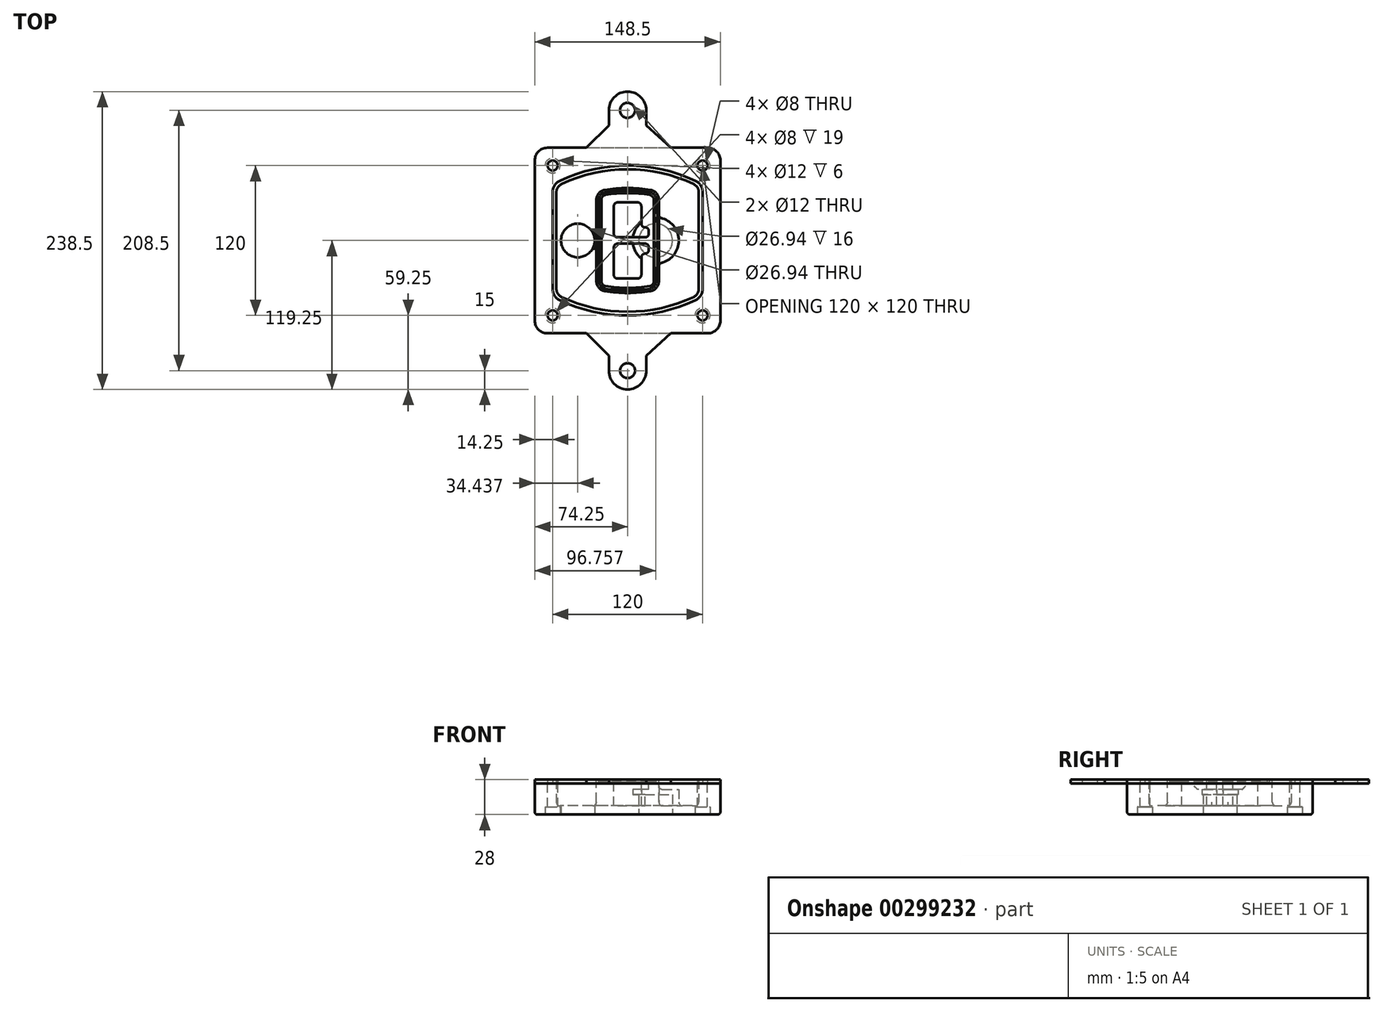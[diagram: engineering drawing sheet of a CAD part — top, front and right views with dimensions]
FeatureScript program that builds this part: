
annotation { "Feature Type Name" : "Feature", "Feature Type Description" : "" }
export const myFeature = defineFeature(function(context is Context, id is Id, definition is map)
    precondition{}
    {
        {
            var Q0;
            Q0=qCreatedBy(makeId("Top.planeOp"),FACE);
            var sketch = newSketch(context, id + "F0", { "sketchPlane" : qUnion([Q0])});
            skPoint(sketch, "E0.rect.middle", {"position": v(0, 0) * mm});
            skLineSegment(sketch, "E1.bottom", {"start": v(-64.25, -74.25) * mm, "end": v(64.25, -74.25) * mm});
            skLineSegment(sketch, "E1.top", {"start": v(-64.25, 74.25) * mm, "end": v(64.25, 74.25) * mm});
            skLineSegment(sketch, "E1.left", {"start": v(-74.25, -64.25) * mm, "end": v(-74.25, 64.25) * mm});
            skLineSegment(sketch, "E1.right", {"start": v(74.25, -64.25) * mm, "end": v(74.25, 64.25) * mm});
            skLineSegment(sketch, "E2", {"start": v(-74.25, 74.25) * mm, "end": v(74.25, -74.25) * mm, "construction": true});
            skLineSegment(sketch, "E3", {"start": v(74.25, 74.25) * mm, "end": v(-74.25, -74.25) * mm, "construction": true});
            skCircle(sketch, "E4", {"center": v(-60, 60) * mm, "radius": 4 * mm});
            skCircle(sketch, "E5", {"center": v(60, 60) * mm, "radius": 4 * mm});
            skCircle(sketch, "E6", {"center": v(60, -60) * mm, "radius": 4 * mm});
            skCircle(sketch, "E7", {"center": v(-60, -60) * mm, "radius": 4 * mm});
            skLineSegment(sketch, "E8", {"start": v(-60, 60) * mm, "end": v(60, 60) * mm, "construction": true});
            skLineSegment(sketch, "E9", {"start": v(60, 60) * mm, "end": v(60, -60) * mm, "construction": true});
            skLineSegment(sketch, "E10", {"start": v(60, -60) * mm, "end": v(-60, -60) * mm, "construction": true});
            skLineSegment(sketch, "E11", {"start": v(-60, -60) * mm, "end": v(-60, 60) * mm, "construction": true});
            skLineSegment(sketch, "E12", {"start": v(-60, 38.83) * mm, "end": v(-60, -38.83) * mm});
            skLineSegment(sketch, "E13", {"start": v(60, 38.83) * mm, "end": v(60, -38.83) * mm});
            skArc(sketch, "E14", {"start": v(54.26, 47.88) * mm, "mid": v(0, 60) * mm, "end": v(-54.26, 47.88) * mm});
            skArc(sketch, "E15", {"start": v(-54.26, -47.88) * mm, "mid": v(0, -60) * mm, "end": v(54.26, -47.88) * mm});
            skLineSegment(sketch, "E16", {"start": v(-60, 0) * mm, "end": v(60, 0) * mm, "construction": true});
            skPoint(sketch, "E17.visualSharp", {"position": v(-60, -45) * mm});
            skArc(sketch, "E17.filletArc", {"start": v(-60, -38.83) * mm, "mid": v(-58.44, -44.2) * mm, "end": v(-54.26, -47.88) * mm});
            skPoint(sketch, "E18.visualSharp", {"position": v(-60, 45) * mm});
            skArc(sketch, "E18.filletArc", {"start": v(-54.26, 47.88) * mm, "mid": v(-58.44, 44.2) * mm, "end": v(-60, 38.83) * mm});
            skPoint(sketch, "E19.visualSharp", {"position": v(60, 45) * mm});
            skArc(sketch, "E19.filletArc", {"start": v(60, 38.83) * mm, "mid": v(58.44, 44.2) * mm, "end": v(54.26, 47.88) * mm});
            skPoint(sketch, "E20.visualSharp", {"position": v(60, -45) * mm});
            skArc(sketch, "E20.filletArc", {"start": v(54.26, -47.88) * mm, "mid": v(58.44, -44.2) * mm, "end": v(60, -38.83) * mm});
            skPoint(sketch, "E21.visualSharp", {"position": v(-74.25, 74.25) * mm});
            skArc(sketch, "E21.filletArc", {"start": v(-64.25, 74.25) * mm, "mid": v(-71.32, 71.32) * mm, "end": v(-74.25, 64.25) * mm});
            skPoint(sketch, "E22.visualSharp", {"position": v(74.25, 74.25) * mm});
            skArc(sketch, "E22.filletArc", {"start": v(74.25, 64.25) * mm, "mid": v(71.32, 71.32) * mm, "end": v(64.25, 74.25) * mm});
            skPoint(sketch, "E23.visualSharp", {"position": v(74.25, -74.25) * mm});
            skArc(sketch, "E23.filletArc", {"start": v(64.25, -74.25) * mm, "mid": v(71.32, -71.32) * mm, "end": v(74.25, -64.25) * mm});
            skPoint(sketch, "E24.visualSharp", {"position": v(-74.25, -74.25) * mm});
            skArc(sketch, "E24.filletArc", {"start": v(-74.25, -64.25) * mm, "mid": v(-71.32, -71.32) * mm, "end": v(-64.25, -74.25) * mm});
            skArc(sketch, "E25.0", {"start": v(57, 38.83) * mm, "mid": v(55.9, 42.58) * mm, "end": v(52.98, 45.17) * mm});
            skLineSegment(sketch, "E25.1", {"start": v(57, 38.83) * mm, "end": v(57, -38.83) * mm});
            skArc(sketch, "E25.2", {"start": v(52.98, -45.17) * mm, "mid": v(55.9, -42.58) * mm, "end": v(57, -38.83) * mm});
            skArc(sketch, "E25.3", {"start": v(-52.98, -45.17) * mm, "mid": v(0, -57) * mm, "end": v(52.98, -45.17) * mm});
            skArc(sketch, "E25.4", {"start": v(-57, -38.83) * mm, "mid": v(-55.9, -42.58) * mm, "end": v(-52.98, -45.17) * mm});
            skArc(sketch, "E25.5", {"start": v(52.98, 45.17) * mm, "mid": v(0, 57) * mm, "end": v(-52.98, 45.17) * mm});
            skLineSegment(sketch, "E25.6", {"start": v(-57, 38.83) * mm, "end": v(-57, -38.83) * mm});
            skArc(sketch, "E25.7", {"start": v(-52.98, 45.17) * mm, "mid": v(-55.9, 42.58) * mm, "end": v(-57, 38.83) * mm});
            skArc(sketch, "E26.0", {"start": v(-55.96, 51.5) * mm, "mid": v(-61.82, 46.33) * mm, "end": v(-64, 38.83) * mm});
            skArc(sketch, "E26.1", {"start": v(55.96, 51.5) * mm, "mid": v(0, 64) * mm, "end": v(-55.96, 51.5) * mm});
            skArc(sketch, "E26.2", {"start": v(64, 38.83) * mm, "mid": v(61.82, 46.33) * mm, "end": v(55.96, 51.5) * mm});
            skLineSegment(sketch, "E26.3", {"start": v(64, 38.83) * mm, "end": v(64, -38.83) * mm});
            skArc(sketch, "E26.4", {"start": v(55.96, -51.5) * mm, "mid": v(61.82, -46.33) * mm, "end": v(64, -38.83) * mm});
            skLineSegment(sketch, "E26.5", {"start": v(-64, 38.83) * mm, "end": v(-64, -38.83) * mm});
            skArc(sketch, "E26.6", {"start": v(-55.96, -51.5) * mm, "mid": v(0, -64) * mm, "end": v(55.96, -51.5) * mm});
            skArc(sketch, "E26.7", {"start": v(-64, -38.83) * mm, "mid": v(-61.82, -46.33) * mm, "end": v(-55.96, -51.5) * mm});
            skSolve(sketch);
        }
        {
            var Q0;
            Q0=makeQuery(id+"F0.imprint","IMPRINT",FACE,{"disambiguationData":[TD([[makeQuery(id+"F0.imprint","IMPRINT",EDGE,{"derivedFrom":sQuery(id+"F0.wireOp",EDGE,"E1.bottom")}),1.0]])]});
            var Q1;
            Q1=makeQuery(id+"F0.imprint","IMPRINT",FACE,{"disambiguationData":[TD([[makeQuery(id+"F0.imprint","IMPRINT",EDGE,{"derivedFrom":sQuery(id+"F0.wireOp",EDGE,"E12")}),1.0]])]});
            var Q2;
            Q2=makeQuery(id+"F0.imprint","IMPRINT",FACE,{"disambiguationData":[TD([[makeQuery(id+"F0.imprint","IMPRINT",EDGE,{"derivedFrom":sQuery(id+"F0.wireOp",EDGE,"E25.0")}),1.0]])]});
            var Q3;
            Q3=makeQuery(id+"F0.imprint","IMPRINT",FACE,{"disambiguationData":[TD([[makeQuery(id+"F0.imprint","IMPRINT",EDGE,{"derivedFrom":sQuery(id+"F0.wireOp",EDGE,"E12")}),-1.0]])]});
            extrude(context, id + "F1", {"entities" : qUnion([Q0, Q1, Q2, Q3]), "oppositeDirection" : true, "depth" : 25 * mm});
        }
        {
            var Q0;
            Q0=makeQuery(id+"F0.imprint","IMPRINT",FACE,{"disambiguationData":[TD([[makeQuery(id+"F0.imprint","IMPRINT",EDGE,{"derivedFrom":sQuery(id+"F0.wireOp",EDGE,"E12")}),1.0]])]});
            extrude(context, id + "F2", {"entities" : qUnion([Q0]), "operationType" : NewBodyOperationType.ADD, "depth" : 3 * mm});
        }
        {
            var Q0;
            Q0=makeQuery(id+"F0.imprint","IMPRINT",FACE,{"disambiguationData":[TD([[makeQuery(id+"F0.imprint","IMPRINT",EDGE,{"derivedFrom":sQuery(id+"F0.wireOp",EDGE,"E25.0")}),1.0]])]});
            extrude(context, id + "F3", {"entities" : qUnion([Q0]), "operationType" : NewBodyOperationType.REMOVE, "oppositeDirection" : true, "depth" : 18 * mm});
        }
        {
            var Q0;
            Q0=makeQuery(id+"F2.opExtrude","CAP_FACE",FACE,{"disambiguationData":[OSD([sQuery(id+"F0.wireOp",EDGE,"E12"),sQuery(id+"F0.wireOp",EDGE,"E13"),sQuery(id+"F0.wireOp",EDGE,"E14"),sQuery(id+"F0.wireOp",EDGE,"E15"),sQuery(id+"F0.wireOp",EDGE,"E17.filletArc"),sQuery(id+"F0.wireOp",EDGE,"E18.filletArc"),sQuery(id+"F0.wireOp",EDGE,"E19.filletArc"),sQuery(id+"F0.wireOp",EDGE,"E20.filletArc"),sQuery(id+"F0.wireOp",EDGE,"E25.0"),sQuery(id+"F0.wireOp",EDGE,"E25.1"),sQuery(id+"F0.wireOp",EDGE,"E25.2"),sQuery(id+"F0.wireOp",EDGE,"E25.3"),sQuery(id+"F0.wireOp",EDGE,"E25.4"),sQuery(id+"F0.wireOp",EDGE,"E25.5"),sQuery(id+"F0.wireOp",EDGE,"E25.6"),sQuery(id+"F0.wireOp",EDGE,"E25.7")])],"isStart":false});
            var sketch = newSketch(context, id + "F4", { "sketchPlane" : qUnion([Q0])});
            skArc(sketch, "E27.0", {"start": v(-18.34, -40.45) * mm, "mid": v(0, -42) * mm, "end": v(18.34, -40.45) * mm});
            skArc(sketch, "E28.0", {"start": v(18.34, 40.45) * mm, "mid": v(0, 42) * mm, "end": v(-18.34, 40.45) * mm});
            skLineSegment(sketch, "E29", {"start": v(-25, 32.57) * mm, "end": v(-25, -32.57) * mm});
            skLineSegment(sketch, "E30", {"start": v(25, 32.57) * mm, "end": v(25, -32.57) * mm});
            skLineSegment(sketch, "E31", {"start": v(-25, 39.1) * mm, "end": v(25, 39.1) * mm, "construction": true});
            skLineSegment(sketch, "E32", {"start": v(-25, -39.1) * mm, "end": v(25, -39.1) * mm, "construction": true});
            skPoint(sketch, "E33.visualSharp", {"position": v(-25, 39.1) * mm});
            skArc(sketch, "E33.filletArc", {"start": v(-18.34, 40.45) * mm, "mid": v(-23.11, 37.73) * mm, "end": v(-25, 32.57) * mm});
            skPoint(sketch, "E34.visualSharp", {"position": v(25, 39.1) * mm});
            skArc(sketch, "E34.filletArc", {"start": v(25, 32.57) * mm, "mid": v(23.11, 37.73) * mm, "end": v(18.34, 40.45) * mm});
            skPoint(sketch, "E35.visualSharp", {"position": v(25, -39.1) * mm});
            skArc(sketch, "E35.filletArc", {"start": v(18.34, -40.45) * mm, "mid": v(23.11, -37.73) * mm, "end": v(25, -32.57) * mm});
            skPoint(sketch, "E36.visualSharp", {"position": v(-25, -39.1) * mm});
            skArc(sketch, "E36.filletArc", {"start": v(-25, -32.57) * mm, "mid": v(-23.11, -37.73) * mm, "end": v(-18.34, -40.45) * mm});
            skArc(sketch, "E37.0", {"start": v(52.98, 45.17) * mm, "mid": v(0, 57) * mm, "end": v(-52.98, 45.17) * mm});
            skArc(sketch, "E37.1", {"start": v(-52.98, 45.17) * mm, "mid": v(-55.9, 42.58) * mm, "end": v(-57, 38.83) * mm});
            skLineSegment(sketch, "E37.2", {"start": v(-57, 38.83) * mm, "end": v(-57, -38.83) * mm});
            skArc(sketch, "E37.3", {"start": v(-57, -38.83) * mm, "mid": v(-55.9, -42.58) * mm, "end": v(-52.98, -45.17) * mm});
            skArc(sketch, "E37.4", {"start": v(-52.98, -45.17) * mm, "mid": v(0, -57) * mm, "end": v(52.98, -45.17) * mm});
            skArc(sketch, "E37.5", {"start": v(52.98, -45.17) * mm, "mid": v(55.9, -42.58) * mm, "end": v(57, -38.83) * mm});
            skLineSegment(sketch, "E37.6", {"start": v(57, 38.83) * mm, "end": v(57, -38.83) * mm});
            skArc(sketch, "E37.7", {"start": v(57, 38.83) * mm, "mid": v(55.9, 42.58) * mm, "end": v(52.98, 45.17) * mm});
            skLineSegment(sketch, "E38.0", {"start": v(23, 32.57) * mm, "end": v(23, -32.57) * mm});
            skArc(sketch, "E38.1", {"start": v(18, -38.48) * mm, "mid": v(21.58, -36.44) * mm, "end": v(23, -32.57) * mm});
            skArc(sketch, "E38.2", {"start": v(-18, -38.48) * mm, "mid": v(0, -40) * mm, "end": v(18, -38.48) * mm});
            skArc(sketch, "E38.3", {"start": v(-23, -32.57) * mm, "mid": v(-21.58, -36.44) * mm, "end": v(-18, -38.48) * mm});
            skLineSegment(sketch, "E38.4", {"start": v(-23, 32.57) * mm, "end": v(-23, -32.57) * mm});
            skArc(sketch, "E38.5", {"start": v(23, 32.57) * mm, "mid": v(21.58, 36.44) * mm, "end": v(18, 38.48) * mm});
            skArc(sketch, "E38.6", {"start": v(-18, 38.48) * mm, "mid": v(-21.58, 36.44) * mm, "end": v(-23, 32.57) * mm});
            skArc(sketch, "E38.7", {"start": v(18, 38.48) * mm, "mid": v(0, 40) * mm, "end": v(-18, 38.48) * mm});
            skArc(sketch, "E39.0", {"start": v(21, 32.57) * mm, "mid": v(20.06, 35.15) * mm, "end": v(17.67, 36.5) * mm});
            skLineSegment(sketch, "E39.1", {"start": v(21, 32.57) * mm, "end": v(21, -32.57) * mm});
            skArc(sketch, "E39.2", {"start": v(17.67, -36.5) * mm, "mid": v(20.06, -35.15) * mm, "end": v(21, -32.57) * mm});
            skArc(sketch, "E39.3", {"start": v(-17.67, -36.5) * mm, "mid": v(0, -38) * mm, "end": v(17.67, -36.5) * mm});
            skArc(sketch, "E39.4", {"start": v(-21, -32.57) * mm, "mid": v(-20.06, -35.15) * mm, "end": v(-17.67, -36.5) * mm});
            skArc(sketch, "E39.5", {"start": v(17.67, 36.5) * mm, "mid": v(0, 38) * mm, "end": v(-17.67, 36.5) * mm});
            skLineSegment(sketch, "E39.6", {"start": v(-21, 32.57) * mm, "end": v(-21, -32.57) * mm});
            skArc(sketch, "E39.7", {"start": v(-17.67, 36.5) * mm, "mid": v(-20.06, 35.15) * mm, "end": v(-21, 32.57) * mm});
            skLineSegment(sketch, "E40", {"start": v(-25, 0) * mm, "end": v(25, 0) * mm, "construction": true});
            skLineSegment(sketch, "E41", {"start": v(-11, 5.5) * mm, "end": v(-11, 27.5) * mm});
            skLineSegment(sketch, "E42", {"start": v(-8, 30.5) * mm, "end": v(8, 30.5) * mm});
            skLineSegment(sketch, "E43", {"start": v(11, 27.5) * mm, "end": v(11, 13.5) * mm});
            skLineSegment(sketch, "E44", {"start": v(14, 10.5) * mm, "end": v(14, 10.5) * mm});
            skLineSegment(sketch, "E45", {"start": v(17, 7.5) * mm, "end": v(17, 5.5) * mm});
            skLineSegment(sketch, "E46", {"start": v(14, 2.5) * mm, "end": v(-8, 2.5) * mm});
            skPoint(sketch, "E47.visualSharp", {"position": v(-11, 30.5) * mm});
            skArc(sketch, "E47.filletArc", {"start": v(-8, 30.5) * mm, "mid": v(-10.12, 29.62) * mm, "end": v(-11, 27.5) * mm});
            skPoint(sketch, "E48.visualSharp", {"position": v(11, 30.5) * mm});
            skArc(sketch, "E48.filletArc", {"start": v(11, 27.5) * mm, "mid": v(10.12, 29.62) * mm, "end": v(8, 30.5) * mm});
            skPoint(sketch, "E49.visualSharp", {"position": v(11, 10.5) * mm});
            skArc(sketch, "E49.filletArc", {"start": v(11, 13.5) * mm, "mid": v(11.88, 11.38) * mm, "end": v(14, 10.5) * mm});
            skPoint(sketch, "E50.visualSharp", {"position": v(17, 10.5) * mm});
            skArc(sketch, "E50.filletArc", {"start": v(17, 7.5) * mm, "mid": v(16.12, 9.62) * mm, "end": v(14, 10.5) * mm});
            skPoint(sketch, "E51.visualSharp", {"position": v(17, 2.5) * mm});
            skArc(sketch, "E51.filletArc", {"start": v(14, 2.5) * mm, "mid": v(16.12, 3.38) * mm, "end": v(17, 5.5) * mm});
            skPoint(sketch, "E52.visualSharp", {"position": v(-11, 2.5) * mm});
            skArc(sketch, "E52.filletArc", {"start": v(-11, 5.5) * mm, "mid": v(-10.12, 3.38) * mm, "end": v(-8, 2.5) * mm});
            skLineSegment(sketch, "E53.0.MirrorCS", {"start": v(14, -2.5) * mm, "end": v(-8, -2.5) * mm});
            skArc(sketch, "E54.0.MirrorCS", {"start": v(-11, -5.5) * mm, "mid": v(-10.12, -3.38) * mm, "end": v(-8, -2.5) * mm});
            skLineSegment(sketch, "E55.0.MirrorCS", {"start": v(-11, -5.5) * mm, "end": v(-11, -27.5) * mm});
            skArc(sketch, "E56.0.MirrorCS", {"start": v(-8, -30.5) * mm, "mid": v(-10.12, -29.62) * mm, "end": v(-11, -27.5) * mm});
            skLineSegment(sketch, "E57.0.MirrorCS", {"start": v(-8, -30.5) * mm, "end": v(8, -30.5) * mm});
            skArc(sketch, "E58.0.MirrorCS", {"start": v(11, -27.5) * mm, "mid": v(10.12, -29.62) * mm, "end": v(8, -30.5) * mm});
            skLineSegment(sketch, "E59.0.MirrorCS", {"start": v(11, -27.5) * mm, "end": v(11, -13.5) * mm});
            skArc(sketch, "E60.0.MirrorCS", {"start": v(11, -13.5) * mm, "mid": v(11.88, -11.38) * mm, "end": v(14, -10.5) * mm});
            skArc(sketch, "E61.0.MirrorCS", {"start": v(17, -7.5) * mm, "mid": v(16.12, -9.62) * mm, "end": v(14, -10.5) * mm});
            skLineSegment(sketch, "E62.0.MirrorCS", {"start": v(17, -7.5) * mm, "end": v(17, -5.5) * mm});
            skArc(sketch, "E63.0.MirrorCS", {"start": v(14, -2.5) * mm, "mid": v(16.12, -3.38) * mm, "end": v(17, -5.5) * mm});
            skSolve(sketch);
        }
        {
            var Q0;
            Q0=makeQuery(id+"F4.imprint","IMPRINT",FACE,{"disambiguationData":[TD([[makeQuery(id+"F4.imprint","IMPRINT",EDGE,{"derivedFrom":sQuery(id+"F4.wireOp",EDGE,"E27.0")}),1.0]])]});
            var Q1;
            Q1=makeQuery(id+"F4.imprint","IMPRINT",FACE,{"disambiguationData":[TD([[makeQuery(id+"F4.imprint","IMPRINT",EDGE,{"derivedFrom":sQuery(id+"F4.wireOp",EDGE,"E38.0")}),-1.0]])]});
            var Q2;
            Q2=makeQuery(id+"F4.imprint","IMPRINT",FACE,{"disambiguationData":[TD([[makeQuery(id+"F4.imprint","IMPRINT",EDGE,{"derivedFrom":sQuery(id+"F4.wireOp",EDGE,"E39.0")}),1.0]])]});
            extrude(context, id + "F5", {"entities" : qUnion([Q0, Q1, Q2]), "operationType" : NewBodyOperationType.ADD, "endBound" : BoundingType.UP_TO_NEXT, "oppositeDirection" : true, "depth" : 25 * mm});
        }
        {
            var Q0;
            Q0=makeQuery(id+"F4.imprint","IMPRINT",FACE,{"disambiguationData":[TD([[makeQuery(id+"F4.imprint","IMPRINT",EDGE,{"derivedFrom":sQuery(id+"F4.wireOp",EDGE,"E38.0")}),-1.0]])]});
            extrude(context, id + "F6", {"entities" : qUnion([Q0]), "operationType" : NewBodyOperationType.REMOVE, "oppositeDirection" : true, "depth" : 2 * mm});
        }
        {
            var Q0;
            Q0=makeQuery(id+"F1.opExtrude","CAP_FACE",FACE,{"disambiguationData":[OSD([sQuery(id+"F0.wireOp",EDGE,"E1.bottom"),sQuery(id+"F0.wireOp",EDGE,"E1.top"),sQuery(id+"F0.wireOp",EDGE,"E1.left"),sQuery(id+"F0.wireOp",EDGE,"E1.right"),sQuery(id+"F0.wireOp",EDGE,"E4"),sQuery(id+"F0.wireOp",EDGE,"E5"),sQuery(id+"F0.wireOp",EDGE,"E6"),sQuery(id+"F0.wireOp",EDGE,"E7"),sQuery(id+"F0.wireOp",EDGE,"E21.filletArc"),sQuery(id+"F0.wireOp",EDGE,"E22.filletArc"),sQuery(id+"F0.wireOp",EDGE,"E23.filletArc"),sQuery(id+"F0.wireOp",EDGE,"E24.filletArc")])],"isStart":false});
            var sketch = newSketch(context, id + "F7", { "sketchPlane" : qUnion([Q0])});
            skCircle(sketch, "E64", {"center": v(22.5, 0) * mm, "radius": 13.47 * mm});
            skCircle(sketch, "E65", {"center": v(-39.81, 0) * mm, "radius": 13.47 * mm});
            skLineSegment(sketch, "E66", {"start": v(74.25, 0) * mm, "end": v(-74.25, 0) * mm});
            skCircle(sketch, "E67", {"center": v(22.5, 0) * mm, "radius": 18.47 * mm});
            skCircle(sketch, "E68", {"center": v(60, -60) * mm, "radius": 6 * mm});
            skCircle(sketch, "E69", {"center": v(-60, -60) * mm, "radius": 6 * mm});
            skCircle(sketch, "E70", {"center": v(-60, 60) * mm, "radius": 6 * mm});
            skCircle(sketch, "E71", {"center": v(60, 60) * mm, "radius": 6 * mm});
            skSolve(sketch);
        }
        {
            var Q0;
            {var subQ1=sQuery(id+"F7.wireOp",EDGE,"E66");var subQ4=sQuery(id+"F7.wireOp",EDGE,"E64");var subQ6=makeQuery(id+"F7.imprint","INTERSECT",VERTEX,{"disambiguationData":[OD(0.0)],"derivedFrom":[subQ4,subQ1]});Q0=makeQuery(id+"F7.imprint","IMPRINT",FACE,{"disambiguationData":[TD([[makeQuery(id+"F7.imprint","IMPRINT",EDGE,{"disambiguationData":[TD([[subQ6,-1.0]])],"derivedFrom":subQ4}),-1.0]])]});}
            var Q1;
            {var subQ0=sQuery(id+"F7.wireOp",EDGE,"E66");var subQ1=sQuery(id+"F7.wireOp",EDGE,"E64");var subQ3=makeQuery(id+"F7.imprint","INTERSECT",VERTEX,{"disambiguationData":[OD(0.0)],"derivedFrom":[subQ1,subQ0]});Q1=makeQuery(id+"F7.imprint","IMPRINT",FACE,{"disambiguationData":[TD([[makeQuery(id+"F7.imprint","IMPRINT",EDGE,{"disambiguationData":[TD([[subQ3,-1.0]])],"derivedFrom":subQ1}),1.0]])]});}
            var Q2;
            {var subQ0=sQuery(id+"F7.wireOp",EDGE,"E66");var subQ1=sQuery(id+"F7.wireOp",EDGE,"E64");var subQ3=makeQuery(id+"F7.imprint","INTERSECT",VERTEX,{"disambiguationData":[OD(0.0)],"derivedFrom":[subQ1,subQ0]});Q2=makeQuery(id+"F7.imprint","IMPRINT",FACE,{"disambiguationData":[TD([[makeQuery(id+"F7.imprint","IMPRINT",EDGE,{"disambiguationData":[TD([[subQ3,1.0]])],"derivedFrom":subQ1}),1.0]])]});}
            var Q3;
            {var subQ1=sQuery(id+"F7.wireOp",EDGE,"E66");var subQ4=sQuery(id+"F7.wireOp",EDGE,"E64");var subQ6=makeQuery(id+"F7.imprint","INTERSECT",VERTEX,{"disambiguationData":[OD(0.0)],"derivedFrom":[subQ4,subQ1]});Q3=makeQuery(id+"F7.imprint","IMPRINT",FACE,{"disambiguationData":[TD([[makeQuery(id+"F7.imprint","IMPRINT",EDGE,{"disambiguationData":[TD([[subQ6,1.0]])],"derivedFrom":subQ4}),-1.0]])]});}
            extrude(context, id + "F8", {"entities" : qUnion([Q0, Q1, Q2, Q3]), "operationType" : NewBodyOperationType.ADD, "oppositeDirection" : true, "depth" : 20 * mm});
        }
        {
            var Q0;
            {var subQ0=sQuery(id+"F7.wireOp",EDGE,"E66");var subQ1=sQuery(id+"F7.wireOp",EDGE,"E64");var subQ3=makeQuery(id+"F7.imprint","INTERSECT",VERTEX,{"disambiguationData":[OD(0.0)],"derivedFrom":[subQ1,subQ0]});Q0=makeQuery(id+"F7.imprint","IMPRINT",FACE,{"disambiguationData":[TD([[makeQuery(id+"F7.imprint","IMPRINT",EDGE,{"disambiguationData":[TD([[subQ3,-1.0]])],"derivedFrom":subQ1}),1.0]])]});}
            var Q1;
            {var subQ0=sQuery(id+"F7.wireOp",EDGE,"E66");var subQ1=sQuery(id+"F7.wireOp",EDGE,"E64");var subQ3=makeQuery(id+"F7.imprint","INTERSECT",VERTEX,{"disambiguationData":[OD(0.0)],"derivedFrom":[subQ1,subQ0]});Q1=makeQuery(id+"F7.imprint","IMPRINT",FACE,{"disambiguationData":[TD([[makeQuery(id+"F7.imprint","IMPRINT",EDGE,{"disambiguationData":[TD([[subQ3,1.0]])],"derivedFrom":subQ1}),1.0]])]});}
            extrude(context, id + "F9", {"entities" : qUnion([Q0, Q1]), "operationType" : NewBodyOperationType.REMOVE, "oppositeDirection" : true, "depth" : 16 * mm});
        }
        {
            var Q0;
            {var subQ0=sQuery(id+"F7.wireOp",EDGE,"E66");var subQ1=sQuery(id+"F7.wireOp",EDGE,"E65");var subQ3=makeQuery(id+"F7.imprint","INTERSECT",VERTEX,{"disambiguationData":[OD(0.0)],"derivedFrom":[subQ1,subQ0]});Q0=makeQuery(id+"F7.imprint","IMPRINT",FACE,{"disambiguationData":[TD([[makeQuery(id+"F7.imprint","IMPRINT",EDGE,{"disambiguationData":[TD([[subQ3,-1.0]])],"derivedFrom":subQ1}),1.0]])]});}
            var Q1;
            {var subQ0=sQuery(id+"F7.wireOp",EDGE,"E66");var subQ1=sQuery(id+"F7.wireOp",EDGE,"E65");var subQ3=makeQuery(id+"F7.imprint","INTERSECT",VERTEX,{"disambiguationData":[OD(0.0)],"derivedFrom":[subQ1,subQ0]});Q1=makeQuery(id+"F7.imprint","IMPRINT",FACE,{"disambiguationData":[TD([[makeQuery(id+"F7.imprint","IMPRINT",EDGE,{"disambiguationData":[TD([[subQ3,1.0]])],"derivedFrom":subQ1}),1.0]])]});}
            extrude(context, id + "F10", {"entities" : qUnion([Q0, Q1]), "operationType" : NewBodyOperationType.REMOVE, "oppositeDirection" : true, "depth" : 25 * mm});
        }
        {
            var Q0;
            Q0=makeQuery(id+"F7.imprint","IMPRINT",FACE,{"disambiguationData":[TD([[makeQuery(id+"F7.imprint","IMPRINT",EDGE,{"derivedFrom":sQuery(id+"F7.wireOp",EDGE,"E68")}),1.0]])]});
            var Q1;
            Q1=makeQuery(id+"F7.imprint","IMPRINT",FACE,{"disambiguationData":[TD([[makeQuery(id+"F7.imprint","IMPRINT",EDGE,{"derivedFrom":makeQuery(id+"F1.opExtrude","CAP_EDGE",EDGE,{"disambiguationData":[OSD([sQuery(id+"F0.wireOp",EDGE,"E5")])],"isStart":false})}),-1.0]])]});
            var Q2;
            Q2=makeQuery(id+"F7.imprint","IMPRINT",FACE,{"disambiguationData":[TD([[makeQuery(id+"F7.imprint","IMPRINT",EDGE,{"derivedFrom":sQuery(id+"F7.wireOp",EDGE,"E69")}),1.0]])]});
            var Q3;
            Q3=makeQuery(id+"F7.imprint","IMPRINT",FACE,{"disambiguationData":[TD([[makeQuery(id+"F7.imprint","IMPRINT",EDGE,{"derivedFrom":makeQuery(id+"F1.opExtrude","CAP_EDGE",EDGE,{"disambiguationData":[OSD([sQuery(id+"F0.wireOp",EDGE,"E4")])],"isStart":false})}),-1.0]])]});
            var Q4;
            Q4=makeQuery(id+"F7.imprint","IMPRINT",FACE,{"disambiguationData":[TD([[makeQuery(id+"F7.imprint","IMPRINT",EDGE,{"derivedFrom":sQuery(id+"F7.wireOp",EDGE,"E70")}),1.0]])]});
            var Q5;
            Q5=makeQuery(id+"F7.imprint","IMPRINT",FACE,{"disambiguationData":[TD([[makeQuery(id+"F7.imprint","IMPRINT",EDGE,{"derivedFrom":makeQuery(id+"F1.opExtrude","CAP_EDGE",EDGE,{"disambiguationData":[OSD([sQuery(id+"F0.wireOp",EDGE,"E7")])],"isStart":false})}),-1.0]])]});
            var Q6;
            Q6=makeQuery(id+"F7.imprint","IMPRINT",FACE,{"disambiguationData":[TD([[makeQuery(id+"F7.imprint","IMPRINT",EDGE,{"derivedFrom":sQuery(id+"F7.wireOp",EDGE,"E71")}),1.0]])]});
            var Q7;
            Q7=makeQuery(id+"F7.imprint","IMPRINT",FACE,{"disambiguationData":[TD([[makeQuery(id+"F7.imprint","IMPRINT",EDGE,{"derivedFrom":makeQuery(id+"F1.opExtrude","CAP_EDGE",EDGE,{"disambiguationData":[OSD([sQuery(id+"F0.wireOp",EDGE,"E6")])],"isStart":false})}),-1.0]])]});
            extrude(context, id + "F11", {"entities" : qUnion([Q0, Q1, Q2, Q3, Q4, Q5, Q6, Q7]), "operationType" : NewBodyOperationType.REMOVE, "oppositeDirection" : true, "depth" : 6 * mm});
        }
        {
            var Q0;
            Q0=makeQuery(id+"F9.boolean.opBoolean","COPY",FACE,{"derivedFrom":makeQuery(id+"F9.opExtrude","CAP_FACE",FACE,{"disambiguationData":[OSD([sQuery(id+"F7.wireOp",EDGE,"E64")])],"isStart":false})});
            var sketch = newSketch(context, id + "F12", { "sketchPlane" : qUnion([Q0])});
            skArc(sketch, "E72.0", {"start": v(11, 14.45) * mm, "mid": v(6.45, 9.13) * mm, "end": v(4.2, 2.5) * mm});
            skArc(sketch, "E72.1", {"start": v(4.2, -2.5) * mm, "mid": v(6.45, -9.13) * mm, "end": v(11, -14.45) * mm});
            skLineSegment(sketch, "E73", {"start": v(4.2, -2.5) * mm, "end": v(14, -2.5) * mm});
            skLineSegment(sketch, "E74.0", {"start": v(14, 2.5) * mm, "end": v(4.2, 2.5) * mm});
            skArc(sketch, "E74.1", {"start": v(14, 2.5) * mm, "mid": v(16.12, 3.38) * mm, "end": v(17, 5.5) * mm});
            skLineSegment(sketch, "E74.2", {"start": v(17, 7.5) * mm, "end": v(17, 5.5) * mm});
            skArc(sketch, "E74.3", {"start": v(17, 7.5) * mm, "mid": v(16.12, 9.62) * mm, "end": v(14, 10.5) * mm});
            skArc(sketch, "E74.4", {"start": v(11, 13.5) * mm, "mid": v(11.88, 11.38) * mm, "end": v(14, 10.5) * mm});
            skLineSegment(sketch, "E74.5", {"start": v(11, 14.45) * mm, "end": v(11, 13.5) * mm});
            skLineSegment(sketch, "E74.7", {"start": v(14, -2.5) * mm, "end": v(4.2, -2.5) * mm});
            skArc(sketch, "E74.8", {"start": v(14, -2.5) * mm, "mid": v(16.12, -3.38) * mm, "end": v(17, -5.5) * mm});
            skLineSegment(sketch, "E74.9", {"start": v(17, -7.5) * mm, "end": v(17, -5.5) * mm});
            skArc(sketch, "E74.10", {"start": v(17, -7.5) * mm, "mid": v(16.12, -9.62) * mm, "end": v(14, -10.5) * mm});
            skArc(sketch, "E74.11", {"start": v(11, -13.5) * mm, "mid": v(11.88, -11.38) * mm, "end": v(14, -10.5) * mm});
            skLineSegment(sketch, "E74.12", {"start": v(11, -14.45) * mm, "end": v(11, -13.5) * mm});
            skPoint(sketch, "E75.orphan", {"position": v(11, -27.5) * mm});
            skPoint(sketch, "E76.orphan", {"position": v(-8, -2.5) * mm});
            skPoint(sketch, "E77.orphan", {"position": v(-8, 2.5) * mm});
            skPoint(sketch, "E78.orphan", {"position": v(11, 27.5) * mm});
            skSolve(sketch);
        }
        {
            var Q0;
            {var subQ7=sQuery(id+"F12.wireOp",EDGE,"E72.0");var subQ14=sQuery(id+"F12.wireOp",EDGE,"E72.1");var subQ16=sQuery(id+"F12.wireOp",EDGE,"E74.1");var subQ18=sQuery(id+"F12.wireOp",EDGE,"E74.8");Q0=qUnion([makeQuery(id+"F12.imprint","IMPRINT",FACE,{"disambiguationData":[TD([[makeQuery(id+"F12.imprint","IMPRINT",EDGE,{"derivedFrom":subQ7}),1.0]])]}),makeQuery(id+"F12.imprint","IMPRINT",FACE,{"disambiguationData":[TD([[makeQuery(id+"F12.imprint","IMPRINT",EDGE,{"derivedFrom":subQ14}),1.0]])]}),makeQuery(id+"F12.imprint","IMPRINT",FACE,{"disambiguationData":[TD([[makeQuery(id+"F12.imprint","IMPRINT",EDGE,{"derivedFrom":subQ16}),1.0]])]}),makeQuery(id+"F12.imprint","IMPRINT",FACE,{"disambiguationData":[TD([[makeQuery(id+"F12.imprint","IMPRINT",EDGE,{"derivedFrom":subQ18}),-1.0]])]})]);}
            var Q1;
            Q1=makeQuery(id+"F5.boolean.opBoolean","SPLIT",FACE,{"disambiguationData":[TD([makeQuery(id+"F5.opExtrude","SWEPT_FACE",FACE,{"disambiguationData":[OSD([sQuery(id+"F4.wireOp",EDGE,"E41")])]})])],"derivedFrom":makeQuery(id+"F3.boolean.opBoolean","COPY",FACE,{"derivedFrom":makeQuery(id+"F3.opExtrude","CAP_FACE",FACE,{"disambiguationData":[OSD([sQuery(id+"F0.wireOp",EDGE,"E25.0"),sQuery(id+"F0.wireOp",EDGE,"E25.1"),sQuery(id+"F0.wireOp",EDGE,"E25.2"),sQuery(id+"F0.wireOp",EDGE,"E25.3"),sQuery(id+"F0.wireOp",EDGE,"E25.4"),sQuery(id+"F0.wireOp",EDGE,"E25.5"),sQuery(id+"F0.wireOp",EDGE,"E25.6"),sQuery(id+"F0.wireOp",EDGE,"E25.7")])],"isStart":false})})});
            extrude(context, id + "F13", {"entities" : qUnion([Q0]), "operationType" : NewBodyOperationType.REMOVE, "endBound" : BoundingType.UP_TO_SURFACE, "endBoundEntityFace" : qUnion([Q1]), "depth" : 25 * mm});
        }
        {
            var Q0;
            Q0=makeQuery(id+"F3.boolean.opBoolean","COPY",EDGE,{"derivedFrom":makeQuery(id+"F3.opExtrude","CAP_EDGE",EDGE,{"disambiguationData":[OSD([sQuery(id+"F0.wireOp",EDGE,"E25.6")])],"isStart":false})});
            var Q1;
            Q1=makeQuery(id+"F8.boolean.opBoolean","INTERSECT",EDGE,{"derivedFrom":[makeQuery(id+"F5.opExtrude","SWEPT_FACE",FACE,{"disambiguationData":[OSD([sQuery(id+"F4.wireOp",EDGE,"E30")])]}),makeQuery(id+"F8.opExtrude","CAP_FACE",FACE,{"disambiguationData":[OSD([sQuery(id+"F7.wireOp",EDGE,"E67")])],"isStart":false})]});
            var Q2;
            Q2=makeQuery(id+"F8.boolean.opBoolean","INTERSECT",EDGE,{"disambiguationData":[OD(1.0)],"derivedFrom":[makeQuery(id+"F5.opExtrude","SWEPT_FACE",FACE,{"disambiguationData":[OSD([sQuery(id+"F4.wireOp",EDGE,"E30")])]}),makeQuery(id+"F8.opExtrude","SWEPT_FACE",FACE,{"disambiguationData":[OSD([sQuery(id+"F7.wireOp",EDGE,"E67")])]})]});
            var Q3;
            {var subQ0=sQuery(id+"F4.wireOp",EDGE,"E30");Q3=makeQuery(id+"F8.boolean.opBoolean","SPLIT",EDGE,{"disambiguationData":[TD([makeQuery(id+"F5.opExtrude","SWEPT_FACE",FACE,{"disambiguationData":[OSD([sQuery(id+"F4.wireOp",EDGE,"E35.filletArc")])]})])],"derivedFrom":makeQuery(id+"F5.opExtrude","CAP_EDGE",EDGE,{"disambiguationData":[OSD([subQ0])],"isStart":false})});}
            var Q4;
            {var subQ0=sQuery(id+"F0.wireOp",EDGE,"E25.7");var subQ1=sQuery(id+"F0.wireOp",EDGE,"E25.1");var subQ2=sQuery(id+"F0.wireOp",EDGE,"E25.6");var subQ3=sQuery(id+"F0.wireOp",EDGE,"E25.5");var subQ4=sQuery(id+"F0.wireOp",EDGE,"E25.4");var subQ5=sQuery(id+"F0.wireOp",EDGE,"E25.0");var subQ6=sQuery(id+"F0.wireOp",EDGE,"E25.2");var subQ7=sQuery(id+"F0.wireOp",EDGE,"E25.3");Q4=makeQuery(id+"F8.boolean.opBoolean","INTERSECT",EDGE,{"derivedFrom":[makeQuery(id+"F5.boolean.opBoolean","SPLIT",FACE,{"disambiguationData":[TD([makeQuery(id+"F2.opExtrude","SWEPT_FACE",FACE,{"disambiguationData":[OSD([subQ5])]})])],"derivedFrom":makeQuery(id+"F3.boolean.opBoolean","COPY",FACE,{"derivedFrom":makeQuery(id+"F3.opExtrude","CAP_FACE",FACE,{"disambiguationData":[OSD([subQ5,subQ1,subQ6,subQ7,subQ4,subQ3,subQ2,subQ0])],"isStart":false})})}),makeQuery(id+"F8.opExtrude","SWEPT_FACE",FACE,{"disambiguationData":[OSD([sQuery(id+"F7.wireOp",EDGE,"E67")])]})]});}
            var Q5;
            Q5=makeQuery(id+"F8.boolean.opBoolean","INTERSECT",EDGE,{"disambiguationData":[OD(0.0)],"derivedFrom":[makeQuery(id+"F5.opExtrude","SWEPT_FACE",FACE,{"disambiguationData":[OSD([sQuery(id+"F4.wireOp",EDGE,"E30")])]}),makeQuery(id+"F8.opExtrude","SWEPT_FACE",FACE,{"disambiguationData":[OSD([sQuery(id+"F7.wireOp",EDGE,"E67")])]})]});
            fillet(context, id + "F14", {"entities" : qUnion([Q0, Q1, Q2, Q3, Q4, Q5]), "radius" : 3 * mm, "tangentPropagation" : true, "allowEdgeOverflow" : false});
        }
        {
            var Q0;
            Q0=makeQuery(id+"F1.opExtrude","CAP_EDGE",EDGE,{"disambiguationData":[OSD([sQuery(id+"F0.wireOp",EDGE,"E1.bottom")])],"isStart":false});
            fillet(context, id + "F15", {"entities" : qUnion([Q0]), "radius" : 2 * mm, "tangentPropagation" : true, "allowEdgeOverflow" : false});
        }
        {
            var Q0;
            {var subQ0=sQuery(id+"F0.wireOp",EDGE,"E21.filletArc");var subQ1=sQuery(id+"F0.wireOp",EDGE,"E7");var subQ2=sQuery(id+"F0.wireOp",EDGE,"E6");var subQ3=sQuery(id+"F0.wireOp",EDGE,"E5");var subQ4=sQuery(id+"F0.wireOp",EDGE,"E4");var subQ5=sQuery(id+"F0.wireOp",EDGE,"E22.filletArc");var subQ6=sQuery(id+"F0.wireOp",EDGE,"E1.bottom");var subQ7=sQuery(id+"F0.wireOp",EDGE,"E1.right");var subQ8=sQuery(id+"F0.wireOp",EDGE,"E1.top");var subQ9=sQuery(id+"F0.wireOp",EDGE,"E1.left");var subQ10=sQuery(id+"F0.wireOp",EDGE,"E23.filletArc");var subQ11=sQuery(id+"F0.wireOp",EDGE,"E24.filletArc");Q0=makeQuery(id+"F2.boolean.opBoolean","SPLIT",FACE,{"disambiguationData":[TD([makeQuery(id+"F1.opExtrude","SWEPT_FACE",FACE,{"disambiguationData":[OSD([subQ6])]})])],"derivedFrom":makeQuery(id+"F1.opExtrude","CAP_FACE",FACE,{"disambiguationData":[OSD([subQ6,subQ8,subQ9,subQ7,subQ4,subQ3,subQ2,subQ1,subQ0,subQ5,subQ10,subQ11])],"isStart":true})});}
            var sketch = newSketch(context, id + "F16", { "sketchPlane" : qUnion([Q0])});
            skLineSegment(sketch, "E79", {"start": v(0, 74.25) * mm, "end": v(0, 104.25) * mm, "construction": true});
            skCircle(sketch, "E80", {"center": v(0, 104.25) * mm, "radius": 6 * mm});
            skArc(sketch, "E81", {"start": v(15, 104.25) * mm, "mid": v(0, 119.25) * mm, "end": v(-15, 104.25) * mm});
            skLineSegment(sketch, "E82", {"start": v(15, 92.25) * mm, "end": v(34.62, 74.25) * mm});
            skLineSegment(sketch, "E83", {"start": v(-15, 92.25) * mm, "end": v(-33, 74.25) * mm});
            skLineSegment(sketch, "E84", {"start": v(-15, 104.25) * mm, "end": v(-15, 92.25) * mm});
            skLineSegment(sketch, "E85", {"start": v(15, 104.25) * mm, "end": v(15, 92.25) * mm});
            skLineSegment(sketch, "E86.MirrorCS", {"start": v(-15, -92.25) * mm, "end": v(-33, -74.25) * mm});
            skLineSegment(sketch, "E87.MirrorCS", {"start": v(15, -92.25) * mm, "end": v(34.62, -74.25) * mm});
            skLineSegment(sketch, "E88.MirrorCS", {"start": v(15, -104.25) * mm, "end": v(15, -92.25) * mm});
            skLineSegment(sketch, "E89.MirrorCS", {"start": v(0, -74.25) * mm, "end": v(0, -104.25) * mm, "construction": true});
            skLineSegment(sketch, "E90.MirrorCS", {"start": v(-15, -104.25) * mm, "end": v(-15, -92.25) * mm});
            skArc(sketch, "E91.MirrorCS", {"start": v(15, -104.25) * mm, "mid": v(0, -119.25) * mm, "end": v(-15, -104.25) * mm});
            skCircle(sketch, "E92.MirrorC", {"center": v(0, -104.25) * mm, "radius": 6 * mm});
            skLineSegment(sketch, "E93", {"start": v(-74.25, 0) * mm, "end": v(74.25, 0) * mm, "construction": true});
            skSolve(sketch);
        }
        {
            var Q0;
            {var subQ1=sQuery(id+"F16.wireOp",EDGE,"E86.MirrorCS");Q0=makeQuery(id+"F16.imprint","IMPRINT",FACE,{"disambiguationData":[TD([[makeQuery(id+"F16.imprint","IMPRINT",EDGE,{"derivedFrom":subQ1}),-1.0]])]});}
            var Q1;
            Q1=makeQuery(id+"F16.imprint","IMPRINT",FACE,{"disambiguationData":[TD([[makeQuery(id+"F16.imprint","IMPRINT",EDGE,{"derivedFrom":sQuery(id+"F16.wireOp",EDGE,"E80")}),-1.0]])]});
            var Q2;
            Q2=makeQuery(id+"F16.imprint","IMPRINT",FACE,{"disambiguationData":[TD([[makeQuery(id+"F16.imprint","IMPRINT",EDGE,{"derivedFrom":makeQuery(id+"F1.opExtrude","CAP_EDGE",EDGE,{"disambiguationData":[OSD([sQuery(id+"F0.wireOp",EDGE,"E1.left")])],"isStart":true})}),-1.0]])]});
            var Q3;
            Q3=makeQuery(id+"F2.opExtrude","CAP_FACE",FACE,{"disambiguationData":[OSD([sQuery(id+"F0.wireOp",EDGE,"E12"),sQuery(id+"F0.wireOp",EDGE,"E13"),sQuery(id+"F0.wireOp",EDGE,"E14"),sQuery(id+"F0.wireOp",EDGE,"E15"),sQuery(id+"F0.wireOp",EDGE,"E17.filletArc"),sQuery(id+"F0.wireOp",EDGE,"E18.filletArc"),sQuery(id+"F0.wireOp",EDGE,"E19.filletArc"),sQuery(id+"F0.wireOp",EDGE,"E20.filletArc"),sQuery(id+"F0.wireOp",EDGE,"E25.0"),sQuery(id+"F0.wireOp",EDGE,"E25.1"),sQuery(id+"F0.wireOp",EDGE,"E25.2"),sQuery(id+"F0.wireOp",EDGE,"E25.3"),sQuery(id+"F0.wireOp",EDGE,"E25.4"),sQuery(id+"F0.wireOp",EDGE,"E25.5"),sQuery(id+"F0.wireOp",EDGE,"E25.6"),sQuery(id+"F0.wireOp",EDGE,"E25.7")])],"isStart":false});
            extrude(context, id + "F17", {"entities" : qUnion([Q0, Q1, Q2]), "endBound" : BoundingType.UP_TO_SURFACE, "endBoundEntityFace" : qUnion([Q3]), "depth" : 25 * mm});
        }
    });
